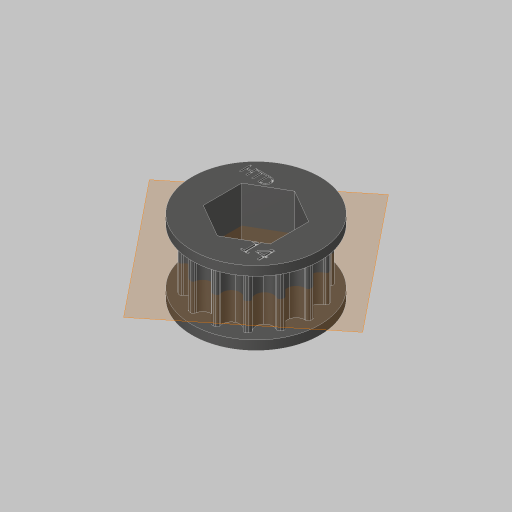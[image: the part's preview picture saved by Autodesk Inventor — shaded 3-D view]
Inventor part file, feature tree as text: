
AUTODESK INVENTOR PART (.ipt)
format: ipt  version: 2023.5 (Build 275446000, 446)  size: 1,166,336 bytes
history: native  units: in
note: dims shown in document units (in); Inventor stores cm internally (conversion verified against a paired STEP export)
features: sketch x5, extrude x4, projected_geometry x2, thicken_offset x1, plane x1, mirror x1, emboss x1, other x1
ambient origin geometry x8: Origin, YZ Plane, XZ Plane, XY Plane, X Axis, Y Axis, Z Axis, Center Point
bodies: Solid1 (feature_tree)
feature tree (16):
  extrude  "spline"  Depth=0.0394in
  thicken_offset  "Thicken1"
  plane  "Work Plane2"
  extrude  "side 1"  Depth=0.0394in
  mirror  "side 2"
  extrude  "spline tol"  Depth=0.0689in
  emboss  "Emboss1"
  extrude  "hex"  TaperAngle=0.0deg  [1 undecoded]
  sketch  "Sketch1"  dims[d0=0.3937in d1=0.0in d3=0.0394in]
  sketch  "Sketch2"  dims[d4=0.0394in d5=0.0625in]
  sketch  "Sketch3"  dims[d6=0.0689in d7=0.0in d8=0.003in]
  sketch  "Sketch4"  dims[d9=0.2339in d10=0.0in d11=0.0in]
  sketch  "Sketch5"  dims[d12=0.0125in d13=0.0in d14=0.502in d15=0.0in d16=0.0in]
  other  "14t HTD Pulley 9.53mm Wide"
  projected_geometry  "Project Cut Edges1"
  projected_geometry  "Project Cut Edges2"
note: 1 required parameter value undecoded (feature->parameter linkage not recoverable at this tier; creation-order binding heuristic only, values carry confidence <= 0.55)
